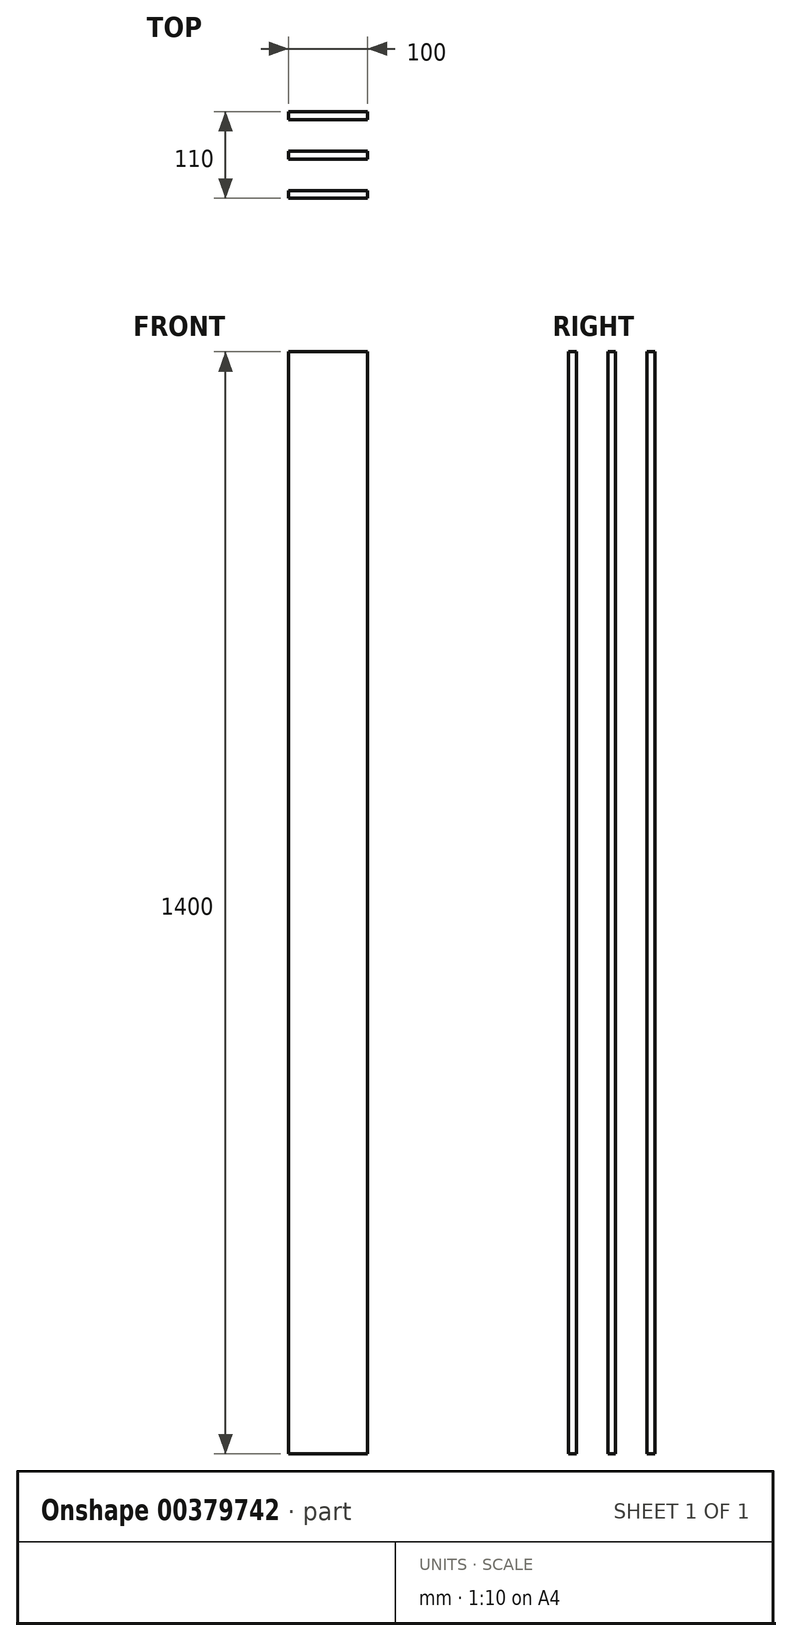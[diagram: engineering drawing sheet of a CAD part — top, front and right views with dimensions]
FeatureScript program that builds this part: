
annotation { "Feature Type Name" : "Feature", "Feature Type Description" : "" }
export const myFeature = defineFeature(function(context is Context, id is Id, definition is map)
    precondition{}
    {
        {
            var Q0;
            Q0=qCreatedBy(makeId("Top.planeOp"),FACE);
            var sketch = newSketch(context, id + "F0", { "sketchPlane" : qUnion([Q0])});
            skLineSegment(sketch, "E0.bottom", {"start": v(50, -5) * mm, "end": v(-50, -5) * mm});
            skLineSegment(sketch, "E0.top", {"start": v(50, 5) * mm, "end": v(-50, 5) * mm});
            skLineSegment(sketch, "E0.left", {"start": v(50, -5) * mm, "end": v(50, 5) * mm});
            skLineSegment(sketch, "E0.right", {"start": v(-50, -5) * mm, "end": v(-50, 5) * mm});
            skPoint(sketch, "E0.middle", {"position": v(0, 0) * mm});
            skLineSegment(sketch, "E1.bottom", {"start": v(50, 55) * mm, "end": v(-50, 55) * mm});
            skLineSegment(sketch, "E1.top", {"start": v(50, 45) * mm, "end": v(-50, 45) * mm});
            skLineSegment(sketch, "E1.left", {"start": v(50, 55) * mm, "end": v(50, 45) * mm});
            skLineSegment(sketch, "E1.right", {"start": v(-50, 55) * mm, "end": v(-50, 45) * mm});
            skPoint(sketch, "E1.middle", {"position": v(0, 50) * mm});
            skLineSegment(sketch, "E2.bottom", {"start": v(50, -55) * mm, "end": v(-50, -55) * mm});
            skLineSegment(sketch, "E2.top", {"start": v(50, -45) * mm, "end": v(-50, -45) * mm});
            skLineSegment(sketch, "E2.left", {"start": v(50, -55) * mm, "end": v(50, -45) * mm});
            skLineSegment(sketch, "E2.right", {"start": v(-50, -55) * mm, "end": v(-50, -45) * mm});
            skPoint(sketch, "E2.middle", {"position": v(0, -50) * mm});
            skLineSegment(sketch, "E3.bottom", {"start": v(20, 5) * mm, "end": v(-20, 5) * mm});
            skLineSegment(sketch, "E3.top", {"start": v(20, 45) * mm, "end": v(-20, 45) * mm});
            skLineSegment(sketch, "E3.left", {"start": v(20, 5) * mm, "end": v(20, 45) * mm});
            skLineSegment(sketch, "E3.right", {"start": v(-20, 5) * mm, "end": v(-20, 45) * mm});
            skPoint(sketch, "E3.middle", {"position": v(0, 25) * mm});
            skLineSegment(sketch, "E4.bottom", {"start": v(20, -45) * mm, "end": v(-20, -45) * mm});
            skLineSegment(sketch, "E4.top", {"start": v(20, -5) * mm, "end": v(-20, -5) * mm});
            skLineSegment(sketch, "E4.left", {"start": v(20, -45) * mm, "end": v(20, -5) * mm});
            skLineSegment(sketch, "E4.right", {"start": v(-20, -45) * mm, "end": v(-20, -5) * mm});
            skPoint(sketch, "E4.middle", {"position": v(0, -25) * mm});
            skSolve(sketch);
        }
        {
            var Q0;
            Q0=makeQuery(id+"F0.imprint","IMPRINT",FACE,{"disambiguationData":[TD([[makeQuery(id+"F0.imprint","IMPRINT",EDGE,{"derivedFrom":sQuery(id+"F0.wireOp",EDGE,"E0.bottom")}),-1.0]])]});
            var Q1;
            Q1=makeQuery(id+"F0.imprint","IMPRINT",FACE,{"disambiguationData":[TD([[makeQuery(id+"F0.imprint","IMPRINT",EDGE,{"derivedFrom":sQuery(id+"F0.wireOp",EDGE,"E3.bottom")}),-1.0]])]});
            var Q2;
            Q2=makeQuery(id+"F0.imprint","IMPRINT",FACE,{"disambiguationData":[TD([[makeQuery(id+"F0.imprint","IMPRINT",EDGE,{"derivedFrom":sQuery(id+"F0.wireOp",EDGE,"E4.bottom")}),-1.0]])]});
            var Q3;
            Q3=makeQuery(id+"F0.imprint","IMPRINT",FACE,{"disambiguationData":[TD([[makeQuery(id+"F0.imprint","IMPRINT",EDGE,{"derivedFrom":sQuery(id+"F0.wireOp",EDGE,"E1.bottom")}),1.0]])]});
            var Q4;
            Q4=makeQuery(id+"F0.imprint","IMPRINT",FACE,{"disambiguationData":[TD([[makeQuery(id+"F0.imprint","IMPRINT",EDGE,{"derivedFrom":sQuery(id+"F0.wireOp",EDGE,"E2.bottom")}),-1.0]])]});
            extrude(context, id + "F1", {"entities" : qUnion([Q0, Q1, Q2, Q3, Q4]), "endBound" : BoundingType.SYMMETRIC, "depth" : 20 * mm});
        }
        {
            var Q0;
            Q0=makeQuery(id+"F1.opExtrude","CAP_FACE",FACE,{"disambiguationData":[OSD([sQuery(id+"F0.wireOp",EDGE,"E0.bottom"),sQuery(id+"F0.wireOp",EDGE,"E0.top"),sQuery(id+"F0.wireOp",EDGE,"E0.left"),sQuery(id+"F0.wireOp",EDGE,"E0.right"),sQuery(id+"F0.wireOp",EDGE,"E1.bottom"),sQuery(id+"F0.wireOp",EDGE,"E1.top"),sQuery(id+"F0.wireOp",EDGE,"E1.left"),sQuery(id+"F0.wireOp",EDGE,"E1.right"),sQuery(id+"F0.wireOp",EDGE,"E2.bottom"),sQuery(id+"F0.wireOp",EDGE,"E2.top"),sQuery(id+"F0.wireOp",EDGE,"E2.left"),sQuery(id+"F0.wireOp",EDGE,"E2.right"),sQuery(id+"F0.wireOp",EDGE,"E3.left"),sQuery(id+"F0.wireOp",EDGE,"E3.right"),sQuery(id+"F0.wireOp",EDGE,"E4.left"),sQuery(id+"F0.wireOp",EDGE,"E4.right")])],"isStart":false});
            var sketch = newSketch(context, id + "F2", { "sketchPlane" : qUnion([Q0])});
            skLineSegment(sketch, "E5.bottom", {"start": v(-50, 5) * mm, "end": v(50, 5) * mm});
            skLineSegment(sketch, "E5.top", {"start": v(-50, -5) * mm, "end": v(50, -5) * mm});
            skLineSegment(sketch, "E5.left", {"start": v(-50, 5) * mm, "end": v(-50, -5) * mm});
            skLineSegment(sketch, "E5.right", {"start": v(50, 5) * mm, "end": v(50, -5) * mm});
            skLineSegment(sketch, "E6.bottom", {"start": v(-50, 55) * mm, "end": v(50, 55) * mm});
            skLineSegment(sketch, "E6.top", {"start": v(-50, 45) * mm, "end": v(50, 45) * mm});
            skLineSegment(sketch, "E6.left", {"start": v(-50, 55) * mm, "end": v(-50, 45) * mm});
            skLineSegment(sketch, "E6.right", {"start": v(50, 55) * mm, "end": v(50, 45) * mm});
            skLineSegment(sketch, "E7.bottom", {"start": v(-50, -45) * mm, "end": v(50, -45) * mm});
            skLineSegment(sketch, "E7.top", {"start": v(-50, -55) * mm, "end": v(50, -55) * mm});
            skLineSegment(sketch, "E7.left", {"start": v(-50, -45) * mm, "end": v(-50, -55) * mm});
            skLineSegment(sketch, "E7.right", {"start": v(50, -45) * mm, "end": v(50, -55) * mm});
            skSolve(sketch);
        }
        {
            var Q0;
            Q0 = qSketchRegion(id + "F2", true);
            extrude(context, id + "F3", {"entities" : qUnion([Q0]), "operationType" : NewBodyOperationType.ADD, "depth" : 690 * mm});
        }
        {
            var Q0;
            Q0=makeQuery(id+"F1.opExtrude","CAP_FACE",FACE,{"disambiguationData":[OSD([sQuery(id+"F0.wireOp",EDGE,"E0.bottom"),sQuery(id+"F0.wireOp",EDGE,"E0.top"),sQuery(id+"F0.wireOp",EDGE,"E0.left"),sQuery(id+"F0.wireOp",EDGE,"E0.right"),sQuery(id+"F0.wireOp",EDGE,"E1.bottom"),sQuery(id+"F0.wireOp",EDGE,"E1.top"),sQuery(id+"F0.wireOp",EDGE,"E1.left"),sQuery(id+"F0.wireOp",EDGE,"E1.right"),sQuery(id+"F0.wireOp",EDGE,"E2.bottom"),sQuery(id+"F0.wireOp",EDGE,"E2.top"),sQuery(id+"F0.wireOp",EDGE,"E2.left"),sQuery(id+"F0.wireOp",EDGE,"E2.right"),sQuery(id+"F0.wireOp",EDGE,"E3.left"),sQuery(id+"F0.wireOp",EDGE,"E3.right"),sQuery(id+"F0.wireOp",EDGE,"E4.left"),sQuery(id+"F0.wireOp",EDGE,"E4.right")])],"isStart":true});
            var sketch = newSketch(context, id + "F4", { "sketchPlane" : qUnion([Q0])});
            skLineSegment(sketch, "E8.bottom", {"start": v(-50, 55) * mm, "end": v(50, 55) * mm});
            skLineSegment(sketch, "E8.top", {"start": v(-50, 45) * mm, "end": v(50, 45) * mm});
            skLineSegment(sketch, "E8.left", {"start": v(-50, 55) * mm, "end": v(-50, 45) * mm});
            skLineSegment(sketch, "E8.right", {"start": v(50, 55) * mm, "end": v(50, 45) * mm});
            skLineSegment(sketch, "E9.bottom", {"start": v(-50, 5) * mm, "end": v(50, 5) * mm});
            skLineSegment(sketch, "E9.top", {"start": v(-50, -5) * mm, "end": v(50, -5) * mm});
            skLineSegment(sketch, "E9.left", {"start": v(-50, 5) * mm, "end": v(-50, -5) * mm});
            skLineSegment(sketch, "E9.right", {"start": v(50, 5) * mm, "end": v(50, -5) * mm});
            skLineSegment(sketch, "E10.bottom", {"start": v(-50, -45) * mm, "end": v(50, -45) * mm});
            skLineSegment(sketch, "E10.top", {"start": v(-50, -55) * mm, "end": v(50, -55) * mm});
            skLineSegment(sketch, "E10.left", {"start": v(-50, -45) * mm, "end": v(-50, -55) * mm});
            skLineSegment(sketch, "E10.right", {"start": v(50, -45) * mm, "end": v(50, -55) * mm});
            skSolve(sketch);
        }
        {
            var Q0;
            Q0 = qSketchRegion(id + "F4", true);
            extrude(context, id + "F5", {"entities" : qUnion([Q0]), "operationType" : NewBodyOperationType.ADD, "depth" : 690 * mm});
        }
    });
